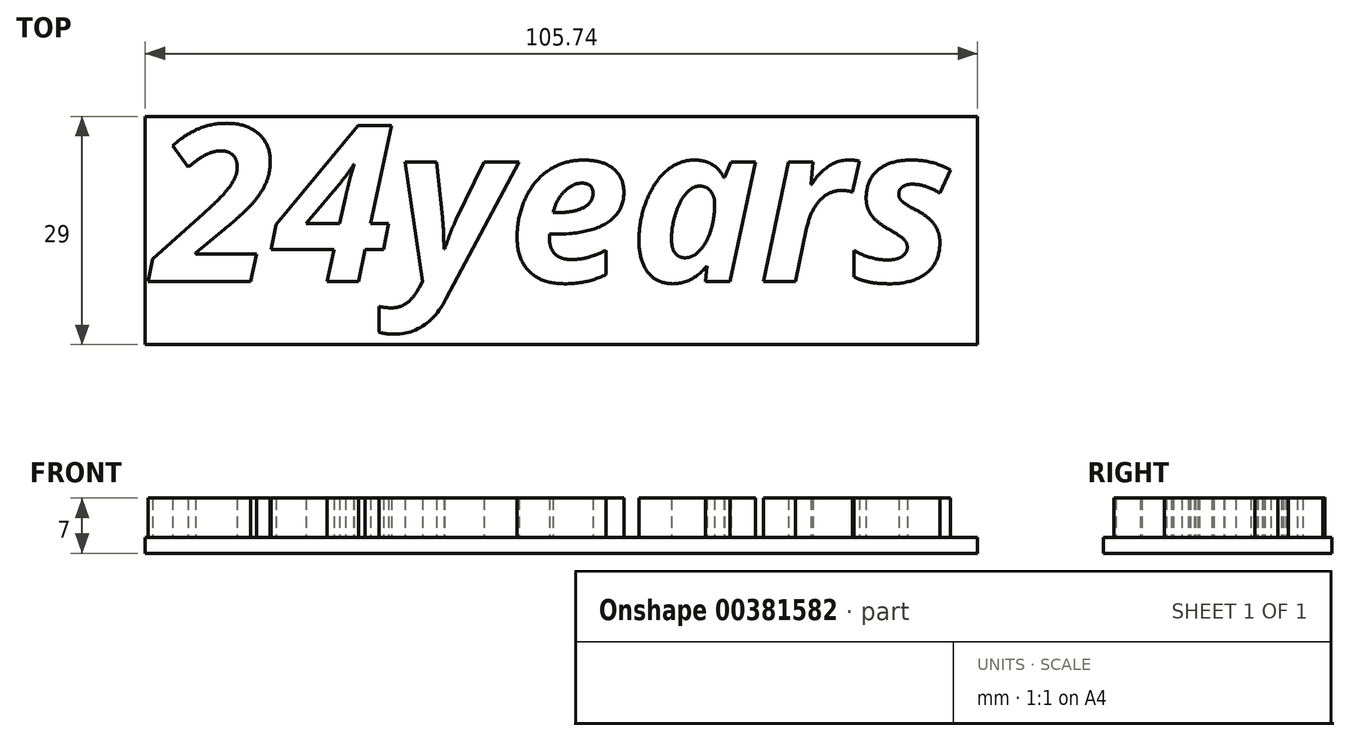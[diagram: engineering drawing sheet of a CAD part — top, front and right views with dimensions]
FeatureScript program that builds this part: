
annotation { "Feature Type Name" : "Feature", "Feature Type Description" : "" }
export const myFeature = defineFeature(function(context is Context, id is Id, definition is map)
    precondition{}
    {
        {
            var Q0;
            Q0=qCreatedBy(makeId("Top.planeOp"),FACE);
            var sketch = newSketch(context, id + "F0", { "sketchPlane" : qUnion([Q0])});
            skText(sketch, "E0", { "text": "24years", "fontName": "OpenSans-BoldItalic.ttf"});
            skPoint(sketch, "E1.middle", {"position": v(0, 0) * mm});
            skPoint(sketch, "E2", {"position": v(0, 10) * mm});
            skLineSegment(sketch, "E3.bottom", {"start": v(-52.87, 21) * mm, "end": v(52.87, 21) * mm});
            skLineSegment(sketch, "E3.top", {"start": v(-52.87, -8) * mm, "end": v(52.87, -8) * mm});
            skLineSegment(sketch, "E3.left", {"start": v(-52.87, 21) * mm, "end": v(-52.87, -8) * mm});
            skLineSegment(sketch, "E3.right", {"start": v(52.87, 21) * mm, "end": v(52.87, -8) * mm});
            const initialGuessF0  = {"E0": [-0.05187, 0, 1, 0, 0.02]};
            skSetInitialGuess(sketch, initialGuessF0);
            skSolve(sketch);
        }
        {
            var Q0;
            Q0=makeQuery(id+"F0.imprint","IMPRINT",FACE,{"disambiguationData":[TD([[makeQuery(id+"F0.imprint","IMPRINT",EDGE,{"derivedFrom":sQuery(id+"F0.wireOp",EDGE,"E0.sketch_text.stroke-43")}),-1.0]])]});
            var Q1;
            Q1=makeQuery(id+"F0.imprint","IMPRINT",FACE,{"disambiguationData":[TD([[makeQuery(id+"F0.imprint","IMPRINT",EDGE,{"derivedFrom":sQuery(id+"F0.wireOp",EDGE,"E0.sketch_text.stroke-50")}),-1.0]])]});
            var Q2;
            Q2=makeQuery(id+"F0.imprint","IMPRINT",FACE,{"disambiguationData":[TD([[makeQuery(id+"F0.imprint","IMPRINT",EDGE,{"derivedFrom":sQuery(id+"F0.wireOp",EDGE,"E0.sketch_text.stroke-0")}),1.0]])]});
            var Q3;
            Q3=makeQuery(id+"F0.imprint","IMPRINT",FACE,{"disambiguationData":[TD([[makeQuery(id+"F0.imprint","IMPRINT",EDGE,{"derivedFrom":sQuery(id+"F0.wireOp",EDGE,"E0.sketch_text.stroke-18")}),-1.0]])]});
            var Q4;
            Q4=makeQuery(id+"F0.imprint","IMPRINT",FACE,{"disambiguationData":[TD([[makeQuery(id+"F0.imprint","IMPRINT",EDGE,{"derivedFrom":sQuery(id+"F0.wireOp",EDGE,"E0.sketch_text.stroke-33")}),1.0]])]});
            var Q5;
            Q5=makeQuery(id+"F0.imprint","IMPRINT",FACE,{"disambiguationData":[TD([[makeQuery(id+"F0.imprint","IMPRINT",EDGE,{"derivedFrom":sQuery(id+"F0.wireOp",EDGE,"E0.sketch_text.stroke-0")}),-1.0]])]});
            var Q6;
            Q6=makeQuery(id+"F0.imprint","IMPRINT",FACE,{"disambiguationData":[TD([[makeQuery(id+"F0.imprint","IMPRINT",EDGE,{"derivedFrom":sQuery(id+"F0.wireOp",EDGE,"E0.sketch_text.stroke-54")}),-1.0]])]});
            var Q7;
            Q7=makeQuery(id+"F0.imprint","IMPRINT",FACE,{"disambiguationData":[TD([[makeQuery(id+"F0.imprint","IMPRINT",EDGE,{"derivedFrom":sQuery(id+"F0.wireOp",EDGE,"E0.sketch_text.stroke-71")}),-1.0]])]});
            var Q8;
            Q8=makeQuery(id+"F0.imprint","IMPRINT",FACE,{"disambiguationData":[TD([[makeQuery(id+"F0.imprint","IMPRINT",EDGE,{"derivedFrom":sQuery(id+"F0.wireOp",EDGE,"E0.sketch_text.stroke-95")}),-1.0]])]});
            var Q9;
            Q9=makeQuery(id+"F0.imprint","IMPRINT",FACE,{"disambiguationData":[TD([[makeQuery(id+"F0.imprint","IMPRINT",EDGE,{"derivedFrom":sQuery(id+"F0.wireOp",EDGE,"E0.sketch_text.stroke-120")}),-1.0]])]});
            var Q10;
            Q10=makeQuery(id+"F0.imprint","IMPRINT",FACE,{"disambiguationData":[TD([[makeQuery(id+"F0.imprint","IMPRINT",EDGE,{"derivedFrom":sQuery(id+"F0.wireOp",EDGE,"E0.sketch_text.stroke-111")}),1.0]])]});
            var Q11;
            Q11=makeQuery(id+"F0.imprint","IMPRINT",FACE,{"disambiguationData":[TD([[makeQuery(id+"F0.imprint","IMPRINT",EDGE,{"derivedFrom":sQuery(id+"F0.wireOp",EDGE,"E0.sketch_text.stroke-120")}),1.0]])]});
            var Q12;
            Q12=makeQuery(id+"F0.imprint","IMPRINT",FACE,{"disambiguationData":[TD([[makeQuery(id+"F0.imprint","IMPRINT",EDGE,{"derivedFrom":sQuery(id+"F0.wireOp",EDGE,"E0.sketch_text.stroke-138")}),-1.0]])]});
            var Q13;
            Q13=makeQuery(id+"F0.imprint","IMPRINT",FACE,{"disambiguationData":[TD([[makeQuery(id+"F0.imprint","IMPRINT",EDGE,{"derivedFrom":sQuery(id+"F0.wireOp",EDGE,"E0.sketch_text.stroke-155")}),-1.0]])]});
            var Q14;
            Q14=makeQuery(id+"F0.imprint","IMPRINT",FACE,{"disambiguationData":[TD([[makeQuery(id+"F0.imprint","IMPRINT",EDGE,{"derivedFrom":sQuery(id+"F0.wireOp",EDGE,"E0.sketch_text.stroke-178")}),-1.0]])]});
            var Q15;
            Q15=makeQuery(id+"F0.imprint","IMPRINT",FACE,{"disambiguationData":[TD([[makeQuery(id+"F0.imprint","IMPRINT",EDGE,{"derivedFrom":sQuery(id+"F0.wireOp",EDGE,"E0.sketch_text.stroke-178")}),1.0]])]});
            var Q16;
            Q16=makeQuery(id+"F0.imprint","IMPRINT",FACE,{"disambiguationData":[TD([[makeQuery(id+"F0.imprint","IMPRINT",EDGE,{"derivedFrom":sQuery(id+"F0.wireOp",EDGE,"E0.sketch_text.stroke-196")}),-1.0]])]});
            var Q17;
            Q17=makeQuery(id+"F0.imprint","IMPRINT",FACE,{"disambiguationData":[TD([[makeQuery(id+"F0.imprint","IMPRINT",EDGE,{"derivedFrom":sQuery(id+"F0.wireOp",EDGE,"E0.sketch_text.stroke-8")}),1.0]])]});
            var Q18;
            Q18=makeQuery(id+"F0.imprint","IMPRINT",FACE,{"disambiguationData":[TD([[makeQuery(id+"F0.imprint","IMPRINT",EDGE,{"derivedFrom":sQuery(id+"F0.wireOp",EDGE,"E0.sketch_text.stroke-16")}),1.0]])]});
            var Q19;
            Q19=makeQuery(id+"F0.imprint","IMPRINT",FACE,{"disambiguationData":[TD([[makeQuery(id+"F0.imprint","IMPRINT",EDGE,{"derivedFrom":sQuery(id+"F0.wireOp",EDGE,"E0.sketch_text.stroke-52")}),1.0]])]});
            var Q20;
            Q20=makeQuery(id+"F0.imprint","IMPRINT",FACE,{"disambiguationData":[TD([[makeQuery(id+"F0.imprint","IMPRINT",EDGE,{"derivedFrom":sQuery(id+"F0.wireOp",EDGE,"E0.sketch_text.stroke-82")}),1.0]])]});
            var Q21;
            Q21=makeQuery(id+"F0.imprint","IMPRINT",FACE,{"disambiguationData":[TD([[makeQuery(id+"F0.imprint","IMPRINT",EDGE,{"derivedFrom":sQuery(id+"F0.wireOp",EDGE,"E0.sketch_text.stroke-146")}),1.0]])]});
            var Q22;
            Q22=makeQuery(id+"F0.imprint","IMPRINT",FACE,{"disambiguationData":[TD([[makeQuery(id+"F0.imprint","IMPRINT",EDGE,{"derivedFrom":sQuery(id+"F0.wireOp",EDGE,"E0.sketch_text.stroke-155")}),1.0]])]});
            var Q23;
            Q23=makeQuery(id+"F0.imprint","IMPRINT",FACE,{"disambiguationData":[TD([[makeQuery(id+"F0.imprint","IMPRINT",EDGE,{"derivedFrom":sQuery(id+"F0.wireOp",EDGE,"E0.sketch_text.stroke-213")}),-1.0]])]});
            var Q24;
            Q24=makeQuery(id+"F0.imprint","IMPRINT",FACE,{"disambiguationData":[TD([[makeQuery(id+"F0.imprint","IMPRINT",EDGE,{"derivedFrom":sQuery(id+"F0.wireOp",EDGE,"E0.sketch_text.stroke-213")}),1.0]])]});
            var Q25;
            Q25=makeQuery(id+"F0.imprint","IMPRINT",FACE,{"disambiguationData":[TD([[makeQuery(id+"F0.imprint","IMPRINT",EDGE,{"derivedFrom":sQuery(id+"F0.wireOp",EDGE,"E0.sketch_text.stroke-231")}),-1.0]])]});
            var Q26;
            Q26=makeQuery(id+"F0.imprint","IMPRINT",FACE,{"disambiguationData":[TD([[makeQuery(id+"F0.imprint","IMPRINT",EDGE,{"derivedFrom":sQuery(id+"F0.wireOp",EDGE,"E0.sketch_text.stroke-23")}),-1.0]])]});
            var Q27;
            Q27=makeQuery(id+"F0.imprint","IMPRINT",FACE,{"disambiguationData":[TD([[makeQuery(id+"F0.imprint","IMPRINT",EDGE,{"derivedFrom":sQuery(id+"F0.wireOp",EDGE,"E0.sketch_text.stroke-62")}),1.0]])]});
            var Q28;
            Q28=makeQuery(id+"F0.imprint","IMPRINT",FACE,{"disambiguationData":[TD([[makeQuery(id+"F0.imprint","IMPRINT",EDGE,{"derivedFrom":sQuery(id+"F0.wireOp",EDGE,"E0.sketch_text.stroke-54")}),1.0]])]});
            var Q29;
            Q29=makeQuery(id+"F0.imprint","IMPRINT",FACE,{"disambiguationData":[TD([[makeQuery(id+"F0.imprint","IMPRINT",EDGE,{"derivedFrom":sQuery(id+"F0.wireOp",EDGE,"E0.sketch_text.stroke-75")}),-1.0]])]});
            var Q30;
            Q30=makeQuery(id+"F0.imprint","IMPRINT",FACE,{"disambiguationData":[TD([[makeQuery(id+"F0.imprint","IMPRINT",EDGE,{"derivedFrom":sQuery(id+"F0.wireOp",EDGE,"E0.sketch_text.stroke-105")}),-1.0]])]});
            var Q31;
            Q31=makeQuery(id+"F0.imprint","IMPRINT",FACE,{"disambiguationData":[TD([[makeQuery(id+"F0.imprint","IMPRINT",EDGE,{"derivedFrom":sQuery(id+"F0.wireOp",EDGE,"E0.sketch_text.stroke-98")}),-1.0]])]});
            var Q32;
            Q32=makeQuery(id+"F0.imprint","IMPRINT",FACE,{"disambiguationData":[TD([[makeQuery(id+"F0.imprint","IMPRINT",EDGE,{"derivedFrom":sQuery(id+"F0.wireOp",EDGE,"E0.sketch_text.stroke-109")}),-1.0]])]});
            var Q33;
            Q33=makeQuery(id+"F0.imprint","IMPRINT",FACE,{"disambiguationData":[TD([[makeQuery(id+"F0.imprint","IMPRINT",EDGE,{"derivedFrom":sQuery(id+"F0.wireOp",EDGE,"E0.sketch_text.stroke-183")}),1.0]])]});
            var Q34;
            Q34=makeQuery(id+"F0.imprint","IMPRINT",FACE,{"disambiguationData":[TD([[makeQuery(id+"F0.imprint","IMPRINT",EDGE,{"derivedFrom":sQuery(id+"F0.wireOp",EDGE,"E0.sketch_text.stroke-192")}),1.0]])]});
            var Q35;
            Q35=makeQuery(id+"F0.imprint","IMPRINT",FACE,{"disambiguationData":[TD([[makeQuery(id+"F0.imprint","IMPRINT",EDGE,{"derivedFrom":sQuery(id+"F0.wireOp",EDGE,"E0.sketch_text.stroke-250")}),-1.0]])]});
            var Q36;
            Q36=makeQuery(id+"F0.imprint","IMPRINT",FACE,{"disambiguationData":[TD([[makeQuery(id+"F0.imprint","IMPRINT",EDGE,{"derivedFrom":sQuery(id+"F0.wireOp",EDGE,"E0.sketch_text.stroke-250")}),1.0]])]});
            var Q37;
            Q37=makeQuery(id+"F0.imprint","IMPRINT",FACE,{"disambiguationData":[TD([[makeQuery(id+"F0.imprint","IMPRINT",EDGE,{"derivedFrom":sQuery(id+"F0.wireOp",EDGE,"E0.sketch_text.stroke-268")}),-1.0]])]});
            var Q38;
            Q38=makeQuery(id+"F0.imprint","IMPRINT",FACE,{"disambiguationData":[TD([[makeQuery(id+"F0.imprint","IMPRINT",EDGE,{"derivedFrom":sQuery(id+"F0.wireOp",EDGE,"E0.sketch_text.stroke-38")}),1.0]])]});
            var Q39;
            Q39=makeQuery(id+"F0.imprint","IMPRINT",FACE,{"disambiguationData":[TD([[makeQuery(id+"F0.imprint","IMPRINT",EDGE,{"derivedFrom":sQuery(id+"F0.wireOp",EDGE,"E0.sketch_text.stroke-56")}),-1.0]])]});
            var Q40;
            Q40=makeQuery(id+"F0.imprint","IMPRINT",FACE,{"disambiguationData":[TD([[makeQuery(id+"F0.imprint","IMPRINT",EDGE,{"derivedFrom":sQuery(id+"F0.wireOp",EDGE,"E0.sketch_text.stroke-241")}),1.0]])]});
            var Q41;
            Q41=makeQuery(id+"F0.imprint","IMPRINT",FACE,{"disambiguationData":[TD([[makeQuery(id+"F0.imprint","IMPRINT",EDGE,{"derivedFrom":sQuery(id+"F0.wireOp",EDGE,"E0.sketch_text.stroke-24")}),-1.0]])]});
            var Q42;
            Q42=makeQuery(id+"F0.imprint","IMPRINT",FACE,{"disambiguationData":[TD([[makeQuery(id+"F0.imprint","IMPRINT",EDGE,{"derivedFrom":sQuery(id+"F0.wireOp",EDGE,"E0.sketch_text.stroke-43")}),1.0]])]});
            var Q43;
            Q43=makeQuery(id+"F0.imprint","IMPRINT",FACE,{"disambiguationData":[TD([[makeQuery(id+"F0.imprint","IMPRINT",EDGE,{"derivedFrom":sQuery(id+"F0.wireOp",EDGE,"E0.sketch_text.stroke-83")}),1.0]])]});
            var Q44;
            Q44=makeQuery(id+"F0.imprint","IMPRINT",FACE,{"disambiguationData":[TD([[makeQuery(id+"F0.imprint","IMPRINT",EDGE,{"derivedFrom":sQuery(id+"F0.wireOp",EDGE,"E0.sketch_text.stroke-123")}),1.0]])]});
            var Q45;
            Q45=makeQuery(id+"F0.imprint","IMPRINT",FACE,{"disambiguationData":[TD([[makeQuery(id+"F0.imprint","IMPRINT",EDGE,{"derivedFrom":sQuery(id+"F0.wireOp",EDGE,"E0.sketch_text.stroke-31")}),-1.0]])]});
            var Q46;
            Q46=makeQuery(id+"F0.imprint","IMPRINT",FACE,{"disambiguationData":[TD([[makeQuery(id+"F0.imprint","IMPRINT",EDGE,{"derivedFrom":sQuery(id+"F0.wireOp",EDGE,"E0.sketch_text.stroke-88")}),-1.0]])]});
            var Q47;
            Q47=makeQuery(id+"F0.imprint","IMPRINT",FACE,{"disambiguationData":[TD([[makeQuery(id+"F0.imprint","IMPRINT",EDGE,{"derivedFrom":sQuery(id+"F0.wireOp",EDGE,"E0.sketch_text.stroke-99")}),-1.0]])]});
            var Q48;
            Q48=makeQuery(id+"F0.imprint","IMPRINT",FACE,{"disambiguationData":[TD([[makeQuery(id+"F0.imprint","IMPRINT",EDGE,{"derivedFrom":sQuery(id+"F0.wireOp",EDGE,"E0.sketch_text.stroke-76")}),-1.0]])]});
            var Q49;
            Q49=makeQuery(id+"F0.imprint","IMPRINT",FACE,{"disambiguationData":[TD([[makeQuery(id+"F0.imprint","IMPRINT",EDGE,{"derivedFrom":sQuery(id+"F0.wireOp",EDGE,"E0.sketch_text.stroke-121")}),-1.0]])]});
            var Q50;
            Q50=makeQuery(id+"F0.imprint","IMPRINT",FACE,{"disambiguationData":[TD([[makeQuery(id+"F0.imprint","IMPRINT",EDGE,{"derivedFrom":sQuery(id+"F0.wireOp",EDGE,"E0.sketch_text.stroke-59")}),-1.0]])]});
            var Q51;
            Q51=makeQuery(id+"F0.imprint","IMPRINT",FACE,{"disambiguationData":[TD([[makeQuery(id+"F0.imprint","IMPRINT",EDGE,{"derivedFrom":sQuery(id+"F0.wireOp",EDGE,"E0.sketch_text.stroke-9")}),1.0]])]});
            var Q52;
            Q52=makeQuery(id+"F0.imprint","IMPRINT",FACE,{"disambiguationData":[TD([[makeQuery(id+"F0.imprint","IMPRINT",EDGE,{"derivedFrom":sQuery(id+"F0.wireOp",EDGE,"E0.sketch_text.stroke-65")}),1.0]])]});
            var Q53;
            Q53=makeQuery(id+"F0.imprint","IMPRINT",FACE,{"disambiguationData":[TD([[makeQuery(id+"F0.imprint","IMPRINT",EDGE,{"derivedFrom":sQuery(id+"F0.wireOp",EDGE,"E0.sketch_text.stroke-158")}),-1.0]])]});
            var Q54;
            Q54=makeQuery(id+"F0.imprint","IMPRINT",FACE,{"disambiguationData":[TD([[makeQuery(id+"F0.imprint","IMPRINT",EDGE,{"derivedFrom":sQuery(id+"F0.wireOp",EDGE,"E0.sketch_text.stroke-164")}),-1.0]])]});
            var Q55;
            Q55=makeQuery(id+"F0.imprint","IMPRINT",FACE,{"disambiguationData":[TD([[makeQuery(id+"F0.imprint","IMPRINT",EDGE,{"derivedFrom":sQuery(id+"F0.wireOp",EDGE,"E0.sketch_text.stroke-99")}),1.0]])]});
            var Q56;
            Q56=makeQuery(id+"F0.imprint","IMPRINT",FACE,{"disambiguationData":[TD([[makeQuery(id+"F0.imprint","IMPRINT",EDGE,{"derivedFrom":sQuery(id+"F0.wireOp",EDGE,"E0.sketch_text.stroke-14")}),-1.0]])]});
            var Q57;
            Q57=makeQuery(id+"F0.imprint","IMPRINT",FACE,{"disambiguationData":[TD([[makeQuery(id+"F0.imprint","IMPRINT",EDGE,{"derivedFrom":sQuery(id+"F0.wireOp",EDGE,"E0.sketch_text.stroke-62")}),-1.0]])]});
            var Q58;
            Q58=makeQuery(id+"F0.imprint","IMPRINT",FACE,{"disambiguationData":[TD([[makeQuery(id+"F0.imprint","IMPRINT",EDGE,{"derivedFrom":sQuery(id+"F0.wireOp",EDGE,"E0.sketch_text.stroke-18")}),1.0]])]});
            var Q59;
            Q59=makeQuery(id+"F0.imprint","IMPRINT",FACE,{"disambiguationData":[TD([[makeQuery(id+"F0.imprint","IMPRINT",EDGE,{"derivedFrom":sQuery(id+"F0.wireOp",EDGE,"E0.sketch_text.stroke-167")}),1.0]])]});
            var Q60;
            Q60=makeQuery(id+"F0.imprint","IMPRINT",FACE,{"disambiguationData":[TD([[makeQuery(id+"F0.imprint","IMPRINT",EDGE,{"derivedFrom":sQuery(id+"F0.wireOp",EDGE,"E0.sketch_text.stroke-159")}),1.0]])]});
            var Q61;
            Q61=makeQuery(id+"F0.imprint","IMPRINT",FACE,{"disambiguationData":[TD([[makeQuery(id+"F0.imprint","IMPRINT",EDGE,{"derivedFrom":sQuery(id+"F0.wireOp",EDGE,"E0.sketch_text.stroke-179")}),-1.0]])]});
            var Q62;
            Q62=makeQuery(id+"F0.imprint","IMPRINT",FACE,{"disambiguationData":[TD([[makeQuery(id+"F0.imprint","IMPRINT",EDGE,{"derivedFrom":sQuery(id+"F0.wireOp",EDGE,"E0.sketch_text.stroke-44")}),-1.0]])]});
            var Q63;
            Q63=makeQuery(id+"F0.imprint","IMPRINT",FACE,{"disambiguationData":[TD([[makeQuery(id+"F0.imprint","IMPRINT",EDGE,{"derivedFrom":sQuery(id+"F0.wireOp",EDGE,"E0.sketch_text.stroke-232")}),-1.0]])]});
            var Q64;
            Q64=makeQuery(id+"F0.imprint","IMPRINT",FACE,{"disambiguationData":[TD([[makeQuery(id+"F0.imprint","IMPRINT",EDGE,{"derivedFrom":sQuery(id+"F0.wireOp",EDGE,"E0.sketch_text.stroke-264")}),1.0]])]});
            var Q65;
            Q65=makeQuery(id+"F0.imprint","IMPRINT",FACE,{"disambiguationData":[TD([[makeQuery(id+"F0.imprint","IMPRINT",EDGE,{"derivedFrom":sQuery(id+"F0.wireOp",EDGE,"E0.sketch_text.stroke-274")}),-1.0]])]});
            var Q66;
            Q66=makeQuery(id+"F0.imprint","IMPRINT",FACE,{"disambiguationData":[TD([[makeQuery(id+"F0.imprint","IMPRINT",EDGE,{"derivedFrom":sQuery(id+"F0.wireOp",EDGE,"E0.sketch_text.stroke-74")}),1.0]])]});
            var Q67;
            Q67=makeQuery(id+"F0.imprint","IMPRINT",FACE,{"disambiguationData":[TD([[makeQuery(id+"F0.imprint","IMPRINT",EDGE,{"derivedFrom":sQuery(id+"F0.wireOp",EDGE,"E0.sketch_text.stroke-180")}),-1.0]])]});
            var Q68;
            Q68=makeQuery(id+"F0.imprint","IMPRINT",FACE,{"disambiguationData":[TD([[makeQuery(id+"F0.imprint","IMPRINT",EDGE,{"derivedFrom":sQuery(id+"F0.wireOp",EDGE,"E0.sketch_text.stroke-33")}),-1.0]])]});
            var Q69;
            Q69=makeQuery(id+"F0.imprint","IMPRINT",FACE,{"disambiguationData":[TD([[makeQuery(id+"F0.imprint","IMPRINT",EDGE,{"derivedFrom":sQuery(id+"F0.wireOp",EDGE,"E0.sketch_text.stroke-84")}),1.0]])]});
            var Q70;
            Q70=makeQuery(id+"F0.imprint","IMPRINT",FACE,{"disambiguationData":[TD([[makeQuery(id+"F0.imprint","IMPRINT",EDGE,{"derivedFrom":sQuery(id+"F0.wireOp",EDGE,"E0.sketch_text.stroke-36")}),-1.0]])]});
            var Q71;
            Q71=makeQuery(id+"F0.imprint","IMPRINT",FACE,{"disambiguationData":[TD([[makeQuery(id+"F0.imprint","IMPRINT",EDGE,{"derivedFrom":sQuery(id+"F0.wireOp",EDGE,"E0.sketch_text.stroke-56")}),1.0]])]});
            extrude(context, id + "F1", {"entities" : qUnion([Q0, Q1, Q2, Q3, Q4, Q5, Q6, Q7, Q8, Q9, Q10, Q11, Q12, Q13, Q14, Q15, Q16, Q17, Q18, Q19, Q20, Q21, Q22, Q23, Q24, Q25, Q26, Q27, Q28, Q29, Q30, Q31, Q32, Q33, Q34, Q35, Q36, Q37, Q38, Q39, Q40, Q41, Q42, Q43, Q44, Q45, Q46, Q47, Q48, Q49, Q50, Q51, Q52, Q53, Q54, Q55, Q56, Q57, Q58, Q59, Q60, Q61, Q62, Q63, Q64, Q65, Q66, Q67, Q68, Q69, Q70, Q71]), "oppositeDirection" : true, "depth" : 2 * mm, "offsetDistance" : 25 * mm});
        }
        {
            var Q0;
            Q0=makeQuery(id+"F0.imprint","IMPRINT",FACE,{"disambiguationData":[TD([[makeQuery(id+"F0.imprint","IMPRINT",EDGE,{"derivedFrom":sQuery(id+"F0.wireOp",EDGE,"E0.sketch_text.stroke-0")}),-1.0]])]});
            var Q1;
            Q1=makeQuery(id+"F0.imprint","IMPRINT",FACE,{"disambiguationData":[TD([[makeQuery(id+"F0.imprint","IMPRINT",EDGE,{"derivedFrom":sQuery(id+"F0.wireOp",EDGE,"E0.sketch_text.stroke-18")}),-1.0]])]});
            var Q2;
            Q2=makeQuery(id+"F0.imprint","IMPRINT",FACE,{"disambiguationData":[TD([[makeQuery(id+"F0.imprint","IMPRINT",EDGE,{"derivedFrom":sQuery(id+"F0.wireOp",EDGE,"E0.sketch_text.stroke-50")}),-1.0]])]});
            var Q3;
            Q3=makeQuery(id+"F0.imprint","IMPRINT",FACE,{"disambiguationData":[TD([[makeQuery(id+"F0.imprint","IMPRINT",EDGE,{"derivedFrom":sQuery(id+"F0.wireOp",EDGE,"E0.sketch_text.stroke-43")}),-1.0]])]});
            var Q4;
            Q4=makeQuery(id+"F0.imprint","IMPRINT",FACE,{"disambiguationData":[TD([[makeQuery(id+"F0.imprint","IMPRINT",EDGE,{"derivedFrom":sQuery(id+"F0.wireOp",EDGE,"E0.sketch_text.stroke-54")}),-1.0]])]});
            var Q5;
            Q5=makeQuery(id+"F0.imprint","IMPRINT",FACE,{"disambiguationData":[TD([[makeQuery(id+"F0.imprint","IMPRINT",EDGE,{"derivedFrom":sQuery(id+"F0.wireOp",EDGE,"E0.sketch_text.stroke-71")}),-1.0]])]});
            var Q6;
            Q6=makeQuery(id+"F0.imprint","IMPRINT",FACE,{"disambiguationData":[TD([[makeQuery(id+"F0.imprint","IMPRINT",EDGE,{"derivedFrom":sQuery(id+"F0.wireOp",EDGE,"E0.sketch_text.stroke-95")}),-1.0]])]});
            var Q7;
            Q7=makeQuery(id+"F0.imprint","IMPRINT",FACE,{"disambiguationData":[TD([[makeQuery(id+"F0.imprint","IMPRINT",EDGE,{"derivedFrom":sQuery(id+"F0.wireOp",EDGE,"E0.sketch_text.stroke-120")}),-1.0]])]});
            var Q8;
            Q8=makeQuery(id+"F0.imprint","IMPRINT",FACE,{"disambiguationData":[TD([[makeQuery(id+"F0.imprint","IMPRINT",EDGE,{"derivedFrom":sQuery(id+"F0.wireOp",EDGE,"E0.sketch_text.stroke-138")}),-1.0]])]});
            var Q9;
            Q9=makeQuery(id+"F0.imprint","IMPRINT",FACE,{"disambiguationData":[TD([[makeQuery(id+"F0.imprint","IMPRINT",EDGE,{"derivedFrom":sQuery(id+"F0.wireOp",EDGE,"E0.sketch_text.stroke-155")}),-1.0]])]});
            var Q10;
            Q10=makeQuery(id+"F0.imprint","IMPRINT",FACE,{"disambiguationData":[TD([[makeQuery(id+"F0.imprint","IMPRINT",EDGE,{"derivedFrom":sQuery(id+"F0.wireOp",EDGE,"E0.sketch_text.stroke-178")}),-1.0]])]});
            var Q11;
            Q11=makeQuery(id+"F0.imprint","IMPRINT",FACE,{"disambiguationData":[TD([[makeQuery(id+"F0.imprint","IMPRINT",EDGE,{"derivedFrom":sQuery(id+"F0.wireOp",EDGE,"E0.sketch_text.stroke-196")}),-1.0]])]});
            var Q12;
            Q12=makeQuery(id+"F0.imprint","IMPRINT",FACE,{"disambiguationData":[TD([[makeQuery(id+"F0.imprint","IMPRINT",EDGE,{"derivedFrom":sQuery(id+"F0.wireOp",EDGE,"E0.sketch_text.stroke-213")}),-1.0]])]});
            var Q13;
            Q13=makeQuery(id+"F0.imprint","IMPRINT",FACE,{"disambiguationData":[TD([[makeQuery(id+"F0.imprint","IMPRINT",EDGE,{"derivedFrom":sQuery(id+"F0.wireOp",EDGE,"E0.sketch_text.stroke-231")}),-1.0]])]});
            var Q14;
            Q14=makeQuery(id+"F0.imprint","IMPRINT",FACE,{"disambiguationData":[TD([[makeQuery(id+"F0.imprint","IMPRINT",EDGE,{"derivedFrom":sQuery(id+"F0.wireOp",EDGE,"E0.sketch_text.stroke-250")}),-1.0]])]});
            var Q15;
            Q15=makeQuery(id+"F0.imprint","IMPRINT",FACE,{"disambiguationData":[TD([[makeQuery(id+"F0.imprint","IMPRINT",EDGE,{"derivedFrom":sQuery(id+"F0.wireOp",EDGE,"E0.sketch_text.stroke-268")}),-1.0]])]});
            var Q16;
            Q16=makeQuery(id+"F0.imprint","IMPRINT",FACE,{"disambiguationData":[TD([[makeQuery(id+"F0.imprint","IMPRINT",EDGE,{"derivedFrom":sQuery(id+"F0.wireOp",EDGE,"E0.sketch_text.stroke-109")}),-1.0]])]});
            var Q17;
            Q17=makeQuery(id+"F0.imprint","IMPRINT",FACE,{"disambiguationData":[TD([[makeQuery(id+"F0.imprint","IMPRINT",EDGE,{"derivedFrom":sQuery(id+"F0.wireOp",EDGE,"E0.sketch_text.stroke-105")}),-1.0]])]});
            var Q18;
            Q18=makeQuery(id+"F0.imprint","IMPRINT",FACE,{"disambiguationData":[TD([[makeQuery(id+"F0.imprint","IMPRINT",EDGE,{"derivedFrom":sQuery(id+"F0.wireOp",EDGE,"E0.sketch_text.stroke-75")}),-1.0]])]});
            var Q19;
            Q19=makeQuery(id+"F0.imprint","IMPRINT",FACE,{"disambiguationData":[TD([[makeQuery(id+"F0.imprint","IMPRINT",EDGE,{"derivedFrom":sQuery(id+"F0.wireOp",EDGE,"E0.sketch_text.stroke-23")}),-1.0]])]});
            var Q20;
            Q20=makeQuery(id+"F0.imprint","IMPRINT",FACE,{"disambiguationData":[TD([[makeQuery(id+"F0.imprint","IMPRINT",EDGE,{"derivedFrom":sQuery(id+"F0.wireOp",EDGE,"E0.sketch_text.stroke-98")}),-1.0]])]});
            var Q21;
            Q21=makeQuery(id+"F0.imprint","IMPRINT",FACE,{"disambiguationData":[TD([[makeQuery(id+"F0.imprint","IMPRINT",EDGE,{"derivedFrom":sQuery(id+"F0.wireOp",EDGE,"E0.sketch_text.stroke-56")}),-1.0]])]});
            var Q22;
            Q22=makeQuery(id+"F0.imprint","IMPRINT",FACE,{"disambiguationData":[TD([[makeQuery(id+"F0.imprint","IMPRINT",EDGE,{"derivedFrom":sQuery(id+"F0.wireOp",EDGE,"E0.sketch_text.stroke-24")}),-1.0]])]});
            var Q23;
            Q23=makeQuery(id+"F0.imprint","IMPRINT",FACE,{"disambiguationData":[TD([[makeQuery(id+"F0.imprint","IMPRINT",EDGE,{"derivedFrom":sQuery(id+"F0.wireOp",EDGE,"E0.sketch_text.stroke-31")}),-1.0]])]});
            var Q24;
            Q24=makeQuery(id+"F0.imprint","IMPRINT",FACE,{"disambiguationData":[TD([[makeQuery(id+"F0.imprint","IMPRINT",EDGE,{"derivedFrom":sQuery(id+"F0.wireOp",EDGE,"E0.sketch_text.stroke-88")}),-1.0]])]});
            var Q25;
            Q25=makeQuery(id+"F0.imprint","IMPRINT",FACE,{"disambiguationData":[TD([[makeQuery(id+"F0.imprint","IMPRINT",EDGE,{"derivedFrom":sQuery(id+"F0.wireOp",EDGE,"E0.sketch_text.stroke-99")}),-1.0]])]});
            var Q26;
            Q26=makeQuery(id+"F0.imprint","IMPRINT",FACE,{"disambiguationData":[TD([[makeQuery(id+"F0.imprint","IMPRINT",EDGE,{"derivedFrom":sQuery(id+"F0.wireOp",EDGE,"E0.sketch_text.stroke-76")}),-1.0]])]});
            var Q27;
            Q27=makeQuery(id+"F0.imprint","IMPRINT",FACE,{"disambiguationData":[TD([[makeQuery(id+"F0.imprint","IMPRINT",EDGE,{"derivedFrom":sQuery(id+"F0.wireOp",EDGE,"E0.sketch_text.stroke-121")}),-1.0]])]});
            var Q28;
            Q28=makeQuery(id+"F0.imprint","IMPRINT",FACE,{"disambiguationData":[TD([[makeQuery(id+"F0.imprint","IMPRINT",EDGE,{"derivedFrom":sQuery(id+"F0.wireOp",EDGE,"E0.sketch_text.stroke-201")}),-1.0]])]});
            var Q29;
            Q29=makeQuery(id+"F0.imprint","IMPRINT",FACE,{"disambiguationData":[TD([[makeQuery(id+"F0.imprint","IMPRINT",EDGE,{"derivedFrom":sQuery(id+"F0.wireOp",EDGE,"E0.sketch_text.stroke-59")}),-1.0]])]});
            var Q30;
            Q30=makeQuery(id+"F0.imprint","IMPRINT",FACE,{"disambiguationData":[TD([[makeQuery(id+"F0.imprint","IMPRINT",EDGE,{"derivedFrom":sQuery(id+"F0.wireOp",EDGE,"E0.sketch_text.stroke-158")}),-1.0]])]});
            var Q31;
            Q31=makeQuery(id+"F0.imprint","IMPRINT",FACE,{"disambiguationData":[TD([[makeQuery(id+"F0.imprint","IMPRINT",EDGE,{"derivedFrom":sQuery(id+"F0.wireOp",EDGE,"E0.sketch_text.stroke-164")}),-1.0]])]});
            var Q32;
            Q32=makeQuery(id+"F0.imprint","IMPRINT",FACE,{"disambiguationData":[TD([[makeQuery(id+"F0.imprint","IMPRINT",EDGE,{"derivedFrom":sQuery(id+"F0.wireOp",EDGE,"E0.sketch_text.stroke-101")}),-1.0]])]});
            var Q33;
            Q33=makeQuery(id+"F0.imprint","IMPRINT",FACE,{"disambiguationData":[TD([[makeQuery(id+"F0.imprint","IMPRINT",EDGE,{"derivedFrom":sQuery(id+"F0.wireOp",EDGE,"E0.sketch_text.stroke-14")}),-1.0]])]});
            var Q34;
            Q34=makeQuery(id+"F0.imprint","IMPRINT",FACE,{"disambiguationData":[TD([[makeQuery(id+"F0.imprint","IMPRINT",EDGE,{"derivedFrom":sQuery(id+"F0.wireOp",EDGE,"E0.sketch_text.stroke-62")}),-1.0]])]});
            var Q35;
            Q35=makeQuery(id+"F0.imprint","IMPRINT",FACE,{"disambiguationData":[TD([[makeQuery(id+"F0.imprint","IMPRINT",EDGE,{"derivedFrom":sQuery(id+"F0.wireOp",EDGE,"E0.sketch_text.stroke-44")}),-1.0]])]});
            var Q36;
            Q36=makeQuery(id+"F0.imprint","IMPRINT",FACE,{"disambiguationData":[TD([[makeQuery(id+"F0.imprint","IMPRINT",EDGE,{"derivedFrom":sQuery(id+"F0.wireOp",EDGE,"E0.sketch_text.stroke-179")}),-1.0]])]});
            var Q37;
            Q37=makeQuery(id+"F0.imprint","IMPRINT",FACE,{"disambiguationData":[TD([[makeQuery(id+"F0.imprint","IMPRINT",EDGE,{"derivedFrom":sQuery(id+"F0.wireOp",EDGE,"E0.sketch_text.stroke-232")}),-1.0]])]});
            var Q38;
            Q38=makeQuery(id+"F0.imprint","IMPRINT",FACE,{"disambiguationData":[TD([[makeQuery(id+"F0.imprint","IMPRINT",EDGE,{"derivedFrom":sQuery(id+"F0.wireOp",EDGE,"E0.sketch_text.stroke-274")}),-1.0]])]});
            var Q39;
            Q39=makeQuery(id+"F0.imprint","IMPRINT",FACE,{"disambiguationData":[TD([[makeQuery(id+"F0.imprint","IMPRINT",EDGE,{"derivedFrom":sQuery(id+"F0.wireOp",EDGE,"E0.sketch_text.stroke-180")}),-1.0]])]});
            var Q40;
            Q40=makeQuery(id+"F0.imprint","IMPRINT",FACE,{"disambiguationData":[TD([[makeQuery(id+"F0.imprint","IMPRINT",EDGE,{"derivedFrom":sQuery(id+"F0.wireOp",EDGE,"E0.sketch_text.stroke-33")}),-1.0]])]});
            var Q41;
            Q41=makeQuery(id+"F0.imprint","IMPRINT",FACE,{"disambiguationData":[TD([[makeQuery(id+"F0.imprint","IMPRINT",EDGE,{"derivedFrom":sQuery(id+"F0.wireOp",EDGE,"E0.sketch_text.stroke-36")}),-1.0]])]});
            extrude(context, id + "F2", {"entities" : qUnion([Q0, Q1, Q2, Q3, Q4, Q5, Q6, Q7, Q8, Q9, Q10, Q11, Q12, Q13, Q14, Q15, Q16, Q17, Q18, Q19, Q20, Q21, Q22, Q23, Q24, Q25, Q26, Q27, Q28, Q29, Q30, Q31, Q32, Q33, Q34, Q35, Q36, Q37, Q38, Q39, Q40, Q41]), "operationType" : NewBodyOperationType.ADD, "depth" : 5 * mm, "offsetDistance" : 25 * mm});
        }
    });
